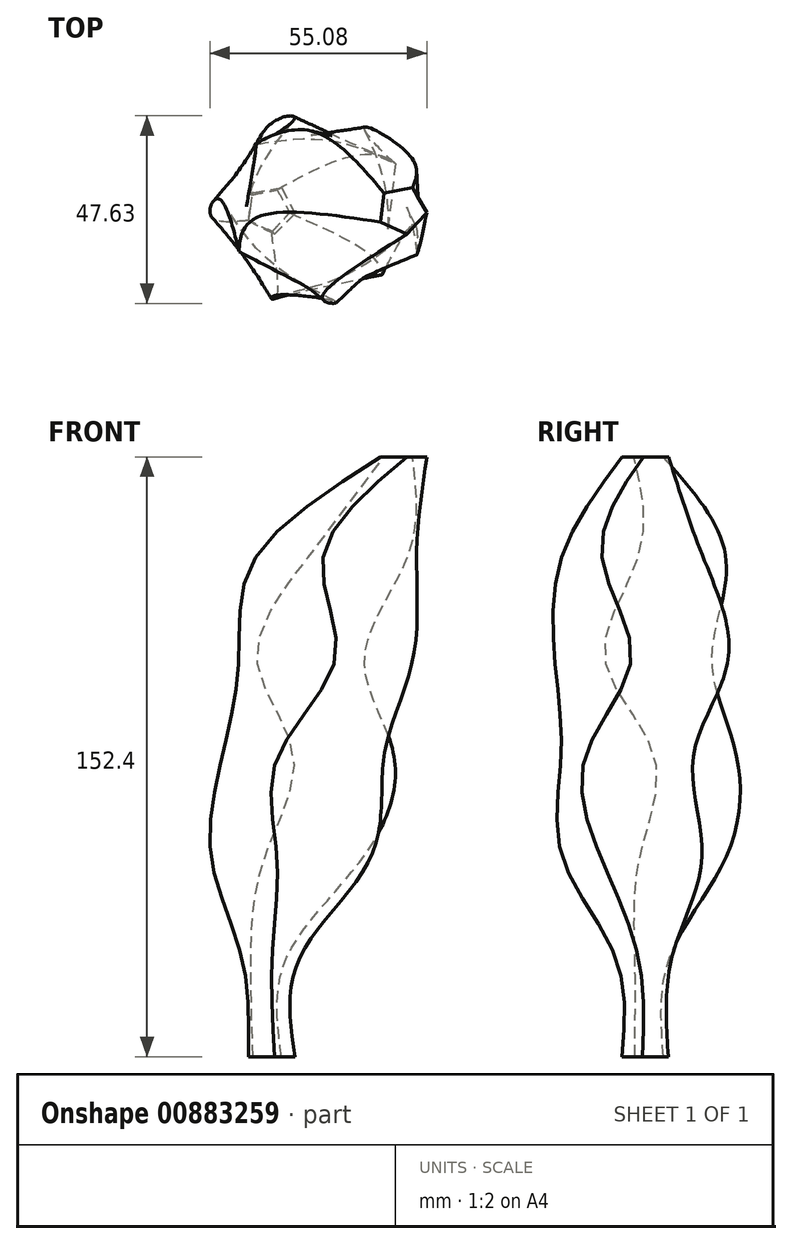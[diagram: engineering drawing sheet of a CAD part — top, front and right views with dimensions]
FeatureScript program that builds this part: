
annotation { "Feature Type Name" : "Feature", "Feature Type Description" : "" }
export const myFeature = defineFeature(function(context is Context, id is Id, definition is map)
    precondition{}
    {
        {
            var Q0;
            Q0=qCreatedBy(makeId("Top.planeOp"),FACE);
            var sketch = newSketch(context, id + "F0", { "sketchPlane" : qUnion([Q0])});
            skCircle(sketch, "E0.cCircle", {"center": v(0, 0) * mm, "radius": 5.08 * mm, "construction": true});
            skLineSegment(sketch, "E0.0", {"start": v(6.2, -0.94) * mm, "end": v(1.03, -6.2) * mm});
            skLineSegment(sketch, "E0.1", {"start": v(1.03, -6.2) * mm, "end": v(-5.57, -2.9) * mm});
            skLineSegment(sketch, "E0.2", {"start": v(-5.57, -2.9) * mm, "end": v(-4.47, 4.4) * mm});
            skLineSegment(sketch, "E0.3", {"start": v(-4.47, 4.4) * mm, "end": v(2.8, 5.62) * mm});
            skLineSegment(sketch, "E0.4", {"start": v(2.8, 5.62) * mm, "end": v(6.2, -0.94) * mm});
            skPoint(sketch, "E0.0.midPoint", {"position": v(3.62, -3.57) * mm});
            skSolve(sketch);
        }
        {
            var Q0;
            Q0=qCreatedBy(makeId("Top.planeOp"),FACE);
            cPlane(context, id + "F1", {"entities" : qUnion([Q0]), "cplaneType" : CPlaneType.OFFSET, "offset" : 25.4 * mm, "width" : 152.4 * mm, "height" : 152.4 * mm});
        }
        {
            var Q0;
            Q0=qCreatedBy(id+"F1.planeOp",FACE);
            var sketch = newSketch(context, id + "F2", { "sketchPlane" : qUnion([Q0])});
            skCircle(sketch, "E1.cCircle", {"center": v(0, 0) * mm, "radius": 6.35 * mm, "construction": true});
            skLineSegment(sketch, "E1.0", {"start": v(7.6, -2) * mm, "end": v(0.45, -7.84) * mm});
            skLineSegment(sketch, "E1.1", {"start": v(0.45, -7.84) * mm, "end": v(-7.32, -2.85) * mm});
            skLineSegment(sketch, "E1.2", {"start": v(-7.32, -2.85) * mm, "end": v(-4.97, 6.08) * mm});
            skLineSegment(sketch, "E1.3", {"start": v(-4.97, 6.08) * mm, "end": v(4.25, 6.6) * mm});
            skLineSegment(sketch, "E1.4", {"start": v(4.25, 6.6) * mm, "end": v(7.6, -2) * mm});
            skPoint(sketch, "E1.0.midPoint", {"position": v(4.02, -4.92) * mm});
            skSolve(sketch);
        }
        {
            var Q0;
            Q0=qCreatedBy(id+"F1.planeOp",FACE);
            cPlane(context, id + "F3", {"entities" : qUnion([Q0]), "cplaneType" : CPlaneType.OFFSET, "offset" : 25.4 * mm, "width" : 152.4 * mm, "height" : 152.4 * mm});
        }
        {
            var Q0;
            Q0=qCreatedBy(id+"F3.planeOp",FACE);
            var sketch = newSketch(context, id + "F4", { "sketchPlane" : qUnion([Q0])});
            skCircle(sketch, "E2.cCircle", {"center": v(6.88, 0) * mm, "radius": 17.78 * mm, "construction": true});
            skLineSegment(sketch, "E2.0", {"start": v(25.56, -11.58) * mm, "end": v(1.64, -21.34) * mm});
            skLineSegment(sketch, "E2.1", {"start": v(1.64, -21.34) * mm, "end": v(-15.04, -1.61) * mm});
            skLineSegment(sketch, "E2.2", {"start": v(-15.04, -1.61) * mm, "end": v(-1.43, 20.35) * mm});
            skLineSegment(sketch, "E2.3", {"start": v(-1.43, 20.35) * mm, "end": v(23.66, 14.19) * mm});
            skLineSegment(sketch, "E2.4", {"start": v(23.66, 14.19) * mm, "end": v(25.56, -11.58) * mm});
            skPoint(sketch, "E2.0.midPoint", {"position": v(13.6, -16.46) * mm});
            skSolve(sketch);
        }
        {
            var Q0;
            Q0=qCreatedBy(id+"F3.planeOp",FACE);
            cPlane(context, id + "F5", {"entities" : qUnion([Q0]), "cplaneType" : CPlaneType.OFFSET, "offset" : 25.4 * mm, "width" : 152.4 * mm, "height" : 152.4 * mm});
        }
        {
            var Q0;
            Q0=qCreatedBy(id+"F5.planeOp",FACE);
            var sketch = newSketch(context, id + "F6", { "sketchPlane" : qUnion([Q0])});
            skCircle(sketch, "E3.cCircle", {"center": v(11.17, 0) * mm, "radius": 19.05 * mm, "construction": true});
            skLineSegment(sketch, "E3.0", {"start": v(28.85, -15.55) * mm, "end": v(1.85, -21.62) * mm});
            skLineSegment(sketch, "E3.1", {"start": v(1.85, -21.62) * mm, "end": v(-12.27, 2.19) * mm});
            skLineSegment(sketch, "E3.2", {"start": v(-12.27, 2.19) * mm, "end": v(6.01, 22.97) * mm});
            skLineSegment(sketch, "E3.3", {"start": v(6.01, 22.97) * mm, "end": v(31.43, 12) * mm});
            skLineSegment(sketch, "E3.4", {"start": v(31.43, 12) * mm, "end": v(28.85, -15.55) * mm});
            skPoint(sketch, "E3.0.midPoint", {"position": v(15.35, -18.59) * mm});
            skSolve(sketch);
        }
        {
            var Q0;
            Q0=qCreatedBy(id+"F5.planeOp",FACE);
            var Q1;
            Q1 = qBodyType(qCreatedBy(id + "F8" ,EDGE), BodyType.WIRE);
            cPlane(context, id + "F7", {"entities" : qUnion([Q0, Q1]), "cplaneType" : CPlaneType.OFFSET, "offset" : 25.4 * mm, "width" : 152.4 * mm, "height" : 152.4 * mm});
        }
        {
            var Q0;
            Q0=qCreatedBy(id+"F7.planeOp",FACE);
            var sketch = newSketch(context, id + "F8", { "sketchPlane" : qUnion([Q0])});
            skCircle(sketch, "E4.cCircle", {"center": v(13.08, 0) * mm, "radius": 19.05 * mm, "construction": true});
            skLineSegment(sketch, "E4.0", {"start": v(-7.97, -10.56) * mm, "end": v(-3.46, 16.76) * mm});
            skLineSegment(sketch, "E4.1", {"start": v(-3.46, 16.76) * mm, "end": v(23.9, 20.91) * mm});
            skLineSegment(sketch, "E4.2", {"start": v(23.9, 20.91) * mm, "end": v(36.31, -3.83) * mm});
            skLineSegment(sketch, "E4.3", {"start": v(36.31, -3.83) * mm, "end": v(16.61, -23.28) * mm});
            skLineSegment(sketch, "E4.4", {"start": v(16.61, -23.28) * mm, "end": v(-7.97, -10.56) * mm});
            skPoint(sketch, "E4.0.midPoint", {"position": v(-5.72, 3.1) * mm});
            skSolve(sketch);
        }
        {
            var Q0;
            Q0=qCreatedBy(id+"F7.planeOp",FACE);
            cPlane(context, id + "F9", {"entities" : qUnion([Q0]), "cplaneType" : CPlaneType.OFFSET, "offset" : 25.4 * mm, "width" : 152.4 * mm, "height" : 152.4 * mm});
        }
        {
            var Q0;
            Q0=qCreatedBy(id+"F9.planeOp",FACE);
            var sketch = newSketch(context, id + "F10", { "sketchPlane" : qUnion([Q0])});
            skCircle(sketch, "E5.cCircle", {"center": v(18.29, 0) * mm, "radius": 17.78 * mm, "construction": true});
            skLineSegment(sketch, "E5.0", {"start": v(-3.6, -1.95) * mm, "end": v(9.66, 20.22) * mm});
            skLineSegment(sketch, "E5.1", {"start": v(9.66, 20.22) * mm, "end": v(34.85, 14.45) * mm});
            skLineSegment(sketch, "E5.2", {"start": v(34.85, 14.45) * mm, "end": v(37.14, -11.29) * mm});
            skLineSegment(sketch, "E5.3", {"start": v(37.14, -11.29) * mm, "end": v(13.38, -21.42) * mm});
            skLineSegment(sketch, "E5.4", {"start": v(13.38, -21.42) * mm, "end": v(-3.6, -1.95) * mm});
            skPoint(sketch, "E5.0.midPoint", {"position": v(3.03, 9.13) * mm});
            skSolve(sketch);
        }
        {
            var Q0;
            Q0=qCreatedBy(id+"F9.planeOp",FACE);
            cPlane(context, id + "F11", {"entities" : qUnion([Q0]), "cplaneType" : CPlaneType.OFFSET, "offset" : 25.4 * mm, "width" : 152.4 * mm, "height" : 152.4 * mm});
        }
        {
            var Q0;
            Q0=qCreatedBy(id+"F11.planeOp",FACE);
            var sketch = newSketch(context, id + "F12", { "sketchPlane" : qUnion([Q0])});
            skCircle(sketch, "E6.cCircle", {"center": v(33.48, 0) * mm, "radius": 5.08 * mm, "construction": true});
            skLineSegment(sketch, "E6.0", {"start": v(28, -3.07) * mm, "end": v(28.86, 4.26) * mm});
            skLineSegment(sketch, "E6.1", {"start": v(28.86, 4.26) * mm, "end": v(36.1, 5.7) * mm});
            skLineSegment(sketch, "E6.2", {"start": v(36.1, 5.7) * mm, "end": v(39.72, -0.73) * mm});
            skLineSegment(sketch, "E6.3", {"start": v(39.72, -0.73) * mm, "end": v(34.71, -6.16) * mm});
            skLineSegment(sketch, "E6.4", {"start": v(34.71, -6.16) * mm, "end": v(28, -3.07) * mm});
            skPoint(sketch, "E6.0.midPoint", {"position": v(28.43, 0.6) * mm});
            skSolve(sketch);
        }
        {
            var Q0;
            Q0=makeQuery(id+"F0.imprint","IMPRINT",FACE,{"disambiguationData":[TD([[makeQuery(id+"F0.imprint","IMPRINT",EDGE,{"derivedFrom":sQuery(id+"F0.wireOp",EDGE,"E0.0")}),-1.0]])]});
            var Q1;
            Q1=makeQuery(id+"F2.imprint","IMPRINT",FACE,{"disambiguationData":[TD([[makeQuery(id+"F2.imprint","IMPRINT",EDGE,{"derivedFrom":sQuery(id+"F2.wireOp",EDGE,"E1.0")}),-1.0]])]});
            var Q2;
            Q2=makeQuery(id+"F4.imprint","IMPRINT",FACE,{"disambiguationData":[TD([[makeQuery(id+"F4.imprint","IMPRINT",EDGE,{"derivedFrom":sQuery(id+"F4.wireOp",EDGE,"E2.0")}),-1.0]])]});
            var Q3;
            Q3=makeQuery(id+"F6.imprint","IMPRINT",FACE,{"disambiguationData":[TD([[makeQuery(id+"F6.imprint","IMPRINT",EDGE,{"derivedFrom":sQuery(id+"F6.wireOp",EDGE,"E3.0")}),-1.0]])]});
            var Q4;
            Q4=makeQuery(id+"F8.imprint","IMPRINT",FACE,{"disambiguationData":[TD([[makeQuery(id+"F8.imprint","IMPRINT",EDGE,{"derivedFrom":sQuery(id+"F8.wireOp",EDGE,"E4.0")}),-1.0]])]});
            var Q5;
            Q5=makeQuery(id+"F10.imprint","IMPRINT",FACE,{"disambiguationData":[TD([[makeQuery(id+"F10.imprint","IMPRINT",EDGE,{"derivedFrom":sQuery(id+"F10.wireOp",EDGE,"E5.0")}),-1.0]])]});
            var Q6;
            Q6=makeQuery(id+"F12.imprint","IMPRINT",FACE,{"disambiguationData":[TD([[makeQuery(id+"F12.imprint","IMPRINT",EDGE,{"derivedFrom":sQuery(id+"F12.wireOp",EDGE,"E6.0")}),-1.0]])]});
            loft(context, id + "F13", {"sheetProfilesArray" : [{ "sheetProfileEntities" : qUnion([Q0]) }, { "sheetProfileEntities" : qUnion([Q1]) }, { "sheetProfileEntities" : qUnion([Q2]) }, { "sheetProfileEntities" : qUnion([Q3]) }, { "sheetProfileEntities" : qUnion([Q4]) }, { "sheetProfileEntities" : qUnion([Q5]) }, { "sheetProfileEntities" : qUnion([Q6]) }]});
        }
    });
